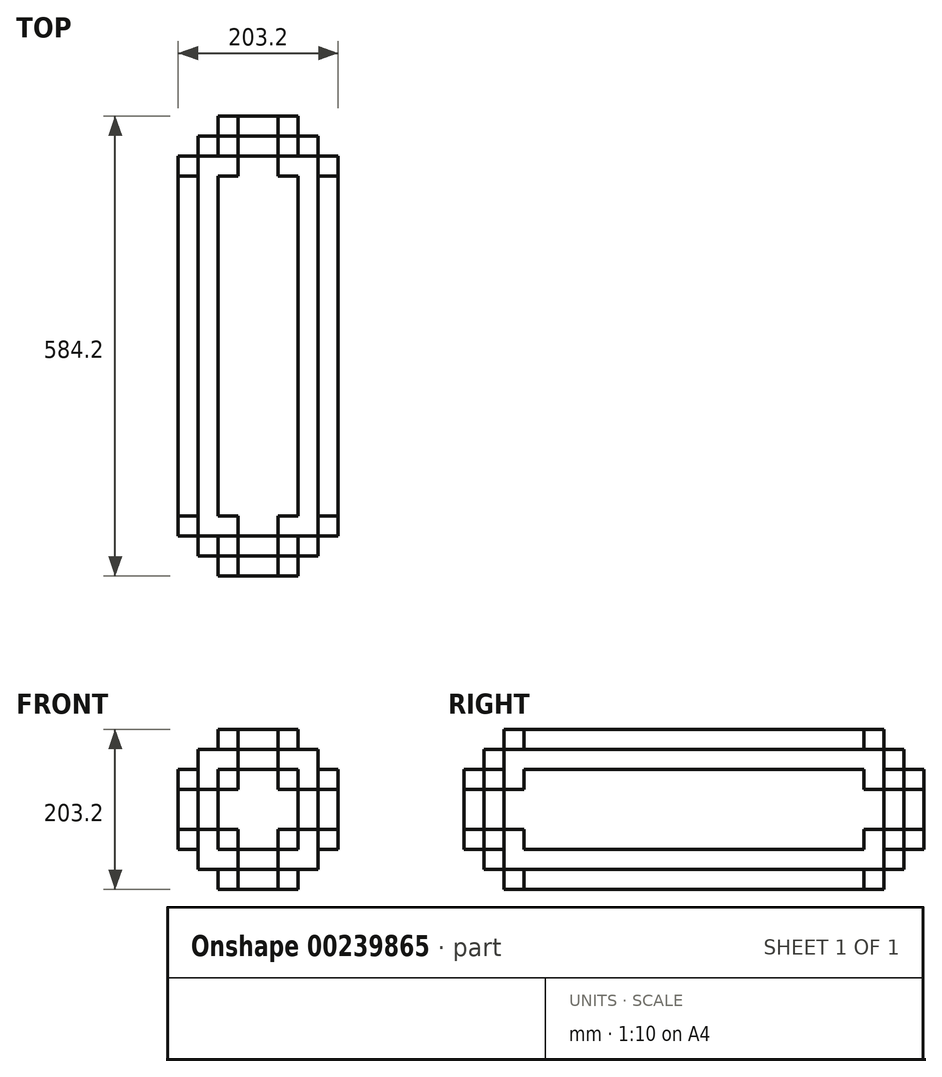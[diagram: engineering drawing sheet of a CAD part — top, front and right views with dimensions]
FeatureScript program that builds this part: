
annotation { "Feature Type Name" : "Feature", "Feature Type Description" : "" }
export const myFeature = defineFeature(function(context is Context, id is Id, definition is map)
    precondition{}
    {
        {
            var Q0;
            Q0=qCreatedBy(makeId("Right.planeOp"),FACE);
            var sketch = newSketch(context, id + "F0", { "sketchPlane" : qUnion([Q0])});
            skLineSegment(sketch, "E0.bottom", {"start": v(38.1, 38.1) * mm, "end": v(-38.1, 38.1) * mm});
            skLineSegment(sketch, "E0.top", {"start": v(38.1, -38.1) * mm, "end": v(-38.1, -38.1) * mm});
            skLineSegment(sketch, "E0.left", {"start": v(38.1, 38.1) * mm, "end": v(38.1, -38.1) * mm});
            skLineSegment(sketch, "E0.right", {"start": v(-38.1, 38.1) * mm, "end": v(-38.1, -38.1) * mm});
            skPoint(sketch, "E0.middle", {"position": v(0, 0) * mm});
            skSolve(sketch);
        }
        {
            var Q0;
            Q0=makeQuery(id+"F0.imprint","IMPRINT",FACE,{"disambiguationData":[TD([[makeQuery(id+"F0.imprint","IMPRINT",EDGE,{"derivedFrom":sQuery(id+"F0.wireOp",EDGE,"E0.bottom")}),1.0]])]});
            extrude(context, id + "F1", {"entities" : qUnion([Q0]), "endBound" : BoundingType.SYMMETRIC, "depth" : 76.2 * mm});
        }
        {
            var Q0;
            Q0=makeQuery(id+"F1.opExtrude","SWEPT_FACE",FACE,{"disambiguationData":[OSD([sQuery(id+"F0.wireOp",EDGE,"E0.bottom")])]});
            var sketch = newSketch(context, id + "F2", { "sketchPlane" : qUnion([Q0])});
            skPoint(sketch, "E1.endSnap0", {"position": v(0, 38.1) * mm});
            skLineSegment(sketch, "E2.bottom", {"start": v(38.1, 38.1) * mm, "end": v(12.7, 38.1) * mm});
            skLineSegment(sketch, "E2.top", {"start": v(38.1, 12.7) * mm, "end": v(12.7, 12.7) * mm});
            skLineSegment(sketch, "E2.left", {"start": v(38.1, 38.1) * mm, "end": v(38.1, 12.7) * mm});
            skLineSegment(sketch, "E2.right", {"start": v(12.7, 38.1) * mm, "end": v(12.7, 12.7) * mm});
            skLineSegment(sketch, "E3.bottom", {"start": v(12.7, 38.1) * mm, "end": v(-12.7, 38.1) * mm});
            skLineSegment(sketch, "E3.top", {"start": v(12.7, 12.7) * mm, "end": v(-12.7, 12.7) * mm});
            skLineSegment(sketch, "E3.right", {"start": v(-12.7, 38.1) * mm, "end": v(-12.7, 12.7) * mm});
            skLineSegment(sketch, "E4.bottom", {"start": v(12.7, 12.7) * mm, "end": v(38.1, 12.7) * mm});
            skLineSegment(sketch, "E4.top", {"start": v(12.7, -12.7) * mm, "end": v(38.1, -12.7) * mm});
            skLineSegment(sketch, "E4.left", {"start": v(12.7, 12.7) * mm, "end": v(12.7, -12.7) * mm});
            skLineSegment(sketch, "E4.right", {"start": v(38.1, 12.7) * mm, "end": v(38.1, -12.7) * mm});
            skSolve(sketch);
        }
        {
            var Q0;
            Q0=makeQuery(id+"F2.imprint","IMPRINT",FACE,{"disambiguationData":[TD([[makeQuery(id+"F2.imprint","IMPRINT",EDGE,{"derivedFrom":sQuery(id+"F2.wireOp",EDGE,"E3.bottom")}),1.0]])]});
            var Q1;
            Q1=makeQuery(id+"F2.imprint","IMPRINT",FACE,{"disambiguationData":[TD([[makeQuery(id+"F2.imprint","IMPRINT",EDGE,{"derivedFrom":sQuery(id+"F2.wireOp",EDGE,"E4.bottom")}),-1.0]])]});
            var Q2;
            Q2=makeQuery(id+"F2.imprint","IMPRINT",FACE,{"disambiguationData":[TD([[makeQuery(id+"F2.imprint","IMPRINT",EDGE,{"derivedFrom":sQuery(id+"F2.wireOp",EDGE,"E2.bottom")}),1.0]])]});
            extrude(context, id + "F3", {"entities" : qUnion([Q0, Q1, Q2]), "operationType" : NewBodyOperationType.REMOVE, "oppositeDirection" : true, "depth" : 25.4 * mm});
        }
        {
            var Q0;
            Q0=makeQuery(id+"F3.boolean.opBoolean","COPY",FACE,{"derivedFrom":makeQuery(id+"F3.opExtrude","CAP_FACE",FACE,{"disambiguationData":[OSD([sQuery(id+"F2.wireOp",EDGE,"E2.bottom"),sQuery(id+"F2.wireOp",EDGE,"E2.left"),sQuery(id+"F2.wireOp",EDGE,"E3.bottom"),sQuery(id+"F2.wireOp",EDGE,"E3.top"),sQuery(id+"F2.wireOp",EDGE,"E3.right"),sQuery(id+"F2.wireOp",EDGE,"E4.top"),sQuery(id+"F2.wireOp",EDGE,"E4.left"),sQuery(id+"F2.wireOp",EDGE,"E4.right")])],"isStart":false})});
            var sketch = newSketch(context, id + "F4", { "sketchPlane" : qUnion([Q0])});
            skLineSegment(sketch, "E5.bottom", {"start": v(38.1, 38.1) * mm, "end": v(12.7, 38.1) * mm});
            skLineSegment(sketch, "E5.top", {"start": v(38.1, 12.7) * mm, "end": v(12.7, 12.7) * mm});
            skLineSegment(sketch, "E5.left", {"start": v(38.1, 38.1) * mm, "end": v(38.1, 12.7) * mm});
            skLineSegment(sketch, "E5.right", {"start": v(12.7, 38.1) * mm, "end": v(12.7, 12.7) * mm});
            skSolve(sketch);
        }
        {
            var Q0;
            Q0=makeQuery(id+"F4.imprint","IMPRINT",FACE,{"disambiguationData":[TD([[makeQuery(id+"F4.imprint","IMPRINT",EDGE,{"derivedFrom":sQuery(id+"F4.wireOp",EDGE,"E5.bottom")}),1.0]])]});
            extrude(context, id + "F5", {"entities" : qUnion([Q0]), "operationType" : NewBodyOperationType.REMOVE, "oppositeDirection" : true, "depth" : 25.4 * mm});
        }
        {
            var Q0;
            Q0=makeQuery(id+"F1.opExtrude","SWEPT_FACE",FACE,{"disambiguationData":[OSD([sQuery(id+"F0.wireOp",EDGE,"E0.left")])]});
            var sketch = newSketch(context, id + "F6", { "sketchPlane" : qUnion([Q0])});
            skLineSegment(sketch, "E6", {"start": v(-12.7, -12.7) * mm, "end": v(-12.7, -38.1) * mm});
            skLineSegment(sketch, "E7", {"start": v(12.7, 12.7) * mm, "end": v(38.1, 12.7) * mm});
            skLineSegment(sketch, "E8.bottom", {"start": v(-12.7, 12.7) * mm, "end": v(12.7, 12.7) * mm});
            skLineSegment(sketch, "E8.top", {"start": v(-12.7, -12.7) * mm, "end": v(12.7, -12.7) * mm});
            skLineSegment(sketch, "E8.left", {"start": v(-12.7, 12.7) * mm, "end": v(-12.7, -12.7) * mm});
            skLineSegment(sketch, "E8.right", {"start": v(12.7, 12.7) * mm, "end": v(12.7, -12.7) * mm});
            skPoint(sketch, "E8.middle", {"position": v(0, 0) * mm});
            skSolve(sketch);
        }
        {
            var Q0;
            {var subQ1=sQuery(id+"F6.wireOp",EDGE,"E6");Q0=makeQuery(id+"F6.imprint","IMPRINT",FACE,{"disambiguationData":[TD([[makeQuery(id+"F6.imprint","IMPRINT",EDGE,{"derivedFrom":subQ1}),1.0]])]});}
            extrude(context, id + "F7", {"entities" : qUnion([Q0]), "operationType" : NewBodyOperationType.ADD, "depth" : 25.4 * mm});
        }
        {
            var Q0;
            Q0=makeQuery(id+"F1.opExtrude","SWEPT_FACE",FACE,{"disambiguationData":[OSD([sQuery(id+"F0.wireOp",EDGE,"E0.bottom")])]});
            var sketch = newSketch(context, id + "F8", { "sketchPlane" : qUnion([Q0])});
            skLineSegment(sketch, "E9.bottom", {"start": v(12.7, 12.7) * mm, "end": v(-12.7, 12.7) * mm});
            skLineSegment(sketch, "E9.top", {"start": v(12.7, -12.7) * mm, "end": v(-12.7, -12.7) * mm});
            skLineSegment(sketch, "E9.left", {"start": v(12.7, 12.7) * mm, "end": v(12.7, -12.7) * mm});
            skLineSegment(sketch, "E9.right", {"start": v(-12.7, 12.7) * mm, "end": v(-12.7, -12.7) * mm});
            skPoint(sketch, "E9.middle", {"position": v(0, 0) * mm});
            skLineSegment(sketch, "E10.bottom", {"start": v(-38.1, 38.1) * mm, "end": v(-12.7, 38.1) * mm});
            skLineSegment(sketch, "E10.top", {"start": v(-38.1, 12.7) * mm, "end": v(-12.7, 12.7) * mm});
            skLineSegment(sketch, "E10.left", {"start": v(-38.1, 38.1) * mm, "end": v(-38.1, 12.7) * mm});
            skLineSegment(sketch, "E10.right", {"start": v(-12.7, 38.1) * mm, "end": v(-12.7, 12.7) * mm});
            skLineSegment(sketch, "E11.bottom", {"start": v(12.7, -12.7) * mm, "end": v(38.1, -12.7) * mm});
            skLineSegment(sketch, "E11.top", {"start": v(12.7, -38.1) * mm, "end": v(38.1, -38.1) * mm});
            skLineSegment(sketch, "E11.left", {"start": v(12.7, -12.7) * mm, "end": v(12.7, -38.1) * mm});
            skLineSegment(sketch, "E11.right", {"start": v(38.1, -12.7) * mm, "end": v(38.1, -38.1) * mm});
            skSolve(sketch);
        }
        {
            var Q0;
            Q0=makeQuery(id+"F8.imprint","IMPRINT",FACE,{"disambiguationData":[TD([[makeQuery(id+"F8.imprint","IMPRINT",EDGE,{"derivedFrom":sQuery(id+"F8.wireOp",EDGE,"E9.top")}),1.0]])]});
            extrude(context, id + "F9", {"entities" : qUnion([Q0]), "operationType" : NewBodyOperationType.ADD, "depth" : 25.4 * mm});
        }
        {
            var Q0;
            Q0=makeQuery(id+"F1.opExtrude","CAP_FACE",FACE,{"disambiguationData":[OSD([sQuery(id+"F0.wireOp",EDGE,"E0.bottom"),sQuery(id+"F0.wireOp",EDGE,"E0.top"),sQuery(id+"F0.wireOp",EDGE,"E0.left"),sQuery(id+"F0.wireOp",EDGE,"E0.right")])],"isStart":false});
            var sketch = newSketch(context, id + "F10", { "sketchPlane" : qUnion([Q0])});
            skLineSegment(sketch, "E12.bottom", {"start": v(-38.1, 38.1) * mm, "end": v(-12.7, 38.1) * mm});
            skLineSegment(sketch, "E12.top", {"start": v(-38.1, 12.7) * mm, "end": v(-12.7, 12.7) * mm});
            skLineSegment(sketch, "E12.left", {"start": v(-38.1, 38.1) * mm, "end": v(-38.1, 12.7) * mm});
            skLineSegment(sketch, "E12.right", {"start": v(-12.7, 38.1) * mm, "end": v(-12.7, 12.7) * mm});
            skLineSegment(sketch, "E13.bottom", {"start": v(12.7, -12.7) * mm, "end": v(38.1, -12.7) * mm});
            skLineSegment(sketch, "E13.top", {"start": v(12.7, -38.1) * mm, "end": v(38.1, -38.1) * mm});
            skLineSegment(sketch, "E13.left", {"start": v(12.7, -12.7) * mm, "end": v(12.7, -38.1) * mm});
            skLineSegment(sketch, "E13.right", {"start": v(38.1, -12.7) * mm, "end": v(38.1, -38.1) * mm});
            skLineSegment(sketch, "E14.bottom", {"start": v(-12.7, 12.7) * mm, "end": v(12.7, 12.7) * mm});
            skLineSegment(sketch, "E14.top", {"start": v(-12.7, -12.7) * mm, "end": v(12.7, -12.7) * mm});
            skLineSegment(sketch, "E14.left", {"start": v(-12.7, 12.7) * mm, "end": v(-12.7, -12.7) * mm});
            skLineSegment(sketch, "E14.right", {"start": v(12.7, 12.7) * mm, "end": v(12.7, -12.7) * mm});
            skSolve(sketch);
        }
        {
            var Q0;
            {var subQ1=sQuery(id+"F10.wireOp",EDGE,"E12.top");Q0=makeQuery(id+"F10.imprint","IMPRINT",FACE,{"disambiguationData":[TD([[makeQuery(id+"F10.imprint","IMPRINT",EDGE,{"derivedFrom":subQ1}),-1.0]])]});}
            extrude(context, id + "F11", {"entities" : qUnion([Q0]), "operationType" : NewBodyOperationType.ADD, "depth" : 25.4 * mm});
        }
        {
            var Q0;
            Q0=makeQuery(id+"F1.opExtrude","SWEPT_BODY",BODY,{"disambiguationData":[OSD([sQuery(id+"F0.wireOp",EDGE,"E0.bottom"),sQuery(id+"F0.wireOp",EDGE,"E0.top"),sQuery(id+"F0.wireOp",EDGE,"E0.left"),sQuery(id+"F0.wireOp",EDGE,"E0.right")])]});
            var Q1;
            {var subQ0=sQuery(id+"F0.wireOp",EDGE,"E0.top");Q1=makeQuery(id+"F11.boolean.opBoolean","MERGE",FACE,{"derivedFrom":[makeQuery(id+"F7.boolean.opBoolean","MERGE",FACE,{"derivedFrom":[makeQuery(id+"F1.opExtrude","SWEPT_FACE",FACE,{"disambiguationData":[OSD([subQ0])]}),makeQuery(id+"F7.opExtrude","SWEPT_FACE",FACE,{"disambiguationData":[OSD([subQ0,sQuery(id+"F0.wireOp",EDGE,"E0.left")])]})]}),makeQuery(id+"F11.opExtrude","SWEPT_FACE",FACE,{"disambiguationData":[OSD([subQ0])]})]});}
            mirror(context, id + "F12", {"operationType" : NewBodyOperationType.ADD, "entities" : qUnion([Q0]), "mirrorPlane" : qUnion([Q1])});
        }
        {
            var Q0;
            Q0=makeQuery(id+"F1.opExtrude","SWEPT_BODY",BODY,{"disambiguationData":[OSD([sQuery(id+"F0.wireOp",EDGE,"E0.bottom"),sQuery(id+"F0.wireOp",EDGE,"E0.top"),sQuery(id+"F0.wireOp",EDGE,"E0.left"),sQuery(id+"F0.wireOp",EDGE,"E0.right")])]});
            var Q1;
            {var subQ0=sQuery(id+"F0.wireOp",EDGE,"E0.bottom");var subQ1=sQuery(id+"F0.wireOp",EDGE,"E0.left");var subQ2=makeQuery(id+"F9.boolean.opBoolean","MERGE",FACE,{"derivedFrom":[makeQuery(id+"F7.boolean.opBoolean","MERGE",FACE,{"derivedFrom":[makeQuery(id+"F1.opExtrude","CAP_FACE",FACE,{"disambiguationData":[OSD([subQ0,sQuery(id+"F0.wireOp",EDGE,"E0.top"),subQ1,sQuery(id+"F0.wireOp",EDGE,"E0.right")])],"isStart":true}),makeQuery(id+"F7.opExtrude","SWEPT_FACE",FACE,{"disambiguationData":[OSD([subQ1])]})]}),makeQuery(id+"F9.opExtrude","SWEPT_FACE",FACE,{"disambiguationData":[OSD([subQ0])]})]});Q1=makeQuery(id+"F12.boolean.opBoolean","MERGE",FACE,{"derivedFrom":[subQ2,makeQuery(id+"F12.opPattern","COPY",FACE,{"derivedFrom":subQ2,"instanceName":"1"})]});}
            mirror(context, id + "F13", {"operationType" : NewBodyOperationType.ADD, "entities" : qUnion([Q0]), "mirrorPlane" : qUnion([Q1])});
        }
        {
            var Q0;
            Q0=qCreatedBy(makeId("Top.planeOp"),FACE);
            var sketch = newSketch(context, id + "F14", { "sketchPlane" : qUnion([Q0])});
            skLineSegment(sketch, "E15", {"start": v(-38.1, -38.1) * mm, "end": v(-38.1, -228.6) * mm});
            skSolve(sketch);
        }
        {
            var Q0;
            {var subQ0=sQuery(id+"F0.wireOp",EDGE,"E0.right");var subQ1=makeQuery(id+"F11.boolean.opBoolean","MERGE",FACE,{"derivedFrom":[makeQuery(id+"F9.boolean.opBoolean","MERGE",FACE,{"derivedFrom":[makeQuery(id+"F1.opExtrude","SWEPT_FACE",FACE,{"disambiguationData":[OSD([subQ0])]}),makeQuery(id+"F9.opExtrude","SWEPT_FACE",FACE,{"disambiguationData":[OSD([sQuery(id+"F0.wireOp",EDGE,"E0.bottom"),subQ0])]})]}),makeQuery(id+"F11.opExtrude","SWEPT_FACE",FACE,{"disambiguationData":[OSD([subQ0])]})]});var subQ2=makeQuery(id+"F12.boolean.opBoolean","MERGE",FACE,{"derivedFrom":[subQ1,makeQuery(id+"F12.opPattern","COPY",FACE,{"derivedFrom":subQ1,"instanceName":"1"})]});Q0=makeQuery(id+"F13.boolean.opBoolean","MERGE",FACE,{"derivedFrom":[subQ2,makeQuery(id+"F13.opPattern","COPY",FACE,{"derivedFrom":subQ2,"instanceName":"1"})]});}
            var Q1;
            Q1=sQuery(id+"F14.wireOp",EDGE,"E15");
            sweep(context, id + "F15", {"operationType" : NewBodyOperationType.ADD, "profiles" : qUnion([Q0]), "path" : qUnion([Q1])});
        }
        {
            var Q0;
            Q0=makeQuery(id+"F1.opExtrude","SWEPT_BODY",BODY,{"disambiguationData":[OSD([sQuery(id+"F0.wireOp",EDGE,"E0.bottom"),sQuery(id+"F0.wireOp",EDGE,"E0.top"),sQuery(id+"F0.wireOp",EDGE,"E0.left"),sQuery(id+"F0.wireOp",EDGE,"E0.right")])]});
            var Q1;
            Q1=makeQuery(id+"F15.opSweep","CAP_FACE",FACE,{"disambiguationData":[OSD([sQuery(id+"F0.wireOp",EDGE,"E0.bottom"),sQuery(id+"F0.wireOp",EDGE,"E0.right"),sQuery(id+"F14.wireOp",VERTEX,"E15.end")])],"isStart":false});
            mirror(context, id + "F16", {"operationType" : NewBodyOperationType.ADD, "entities" : qUnion([Q0]), "mirrorPlane" : qUnion([Q1])});
        }
    });
